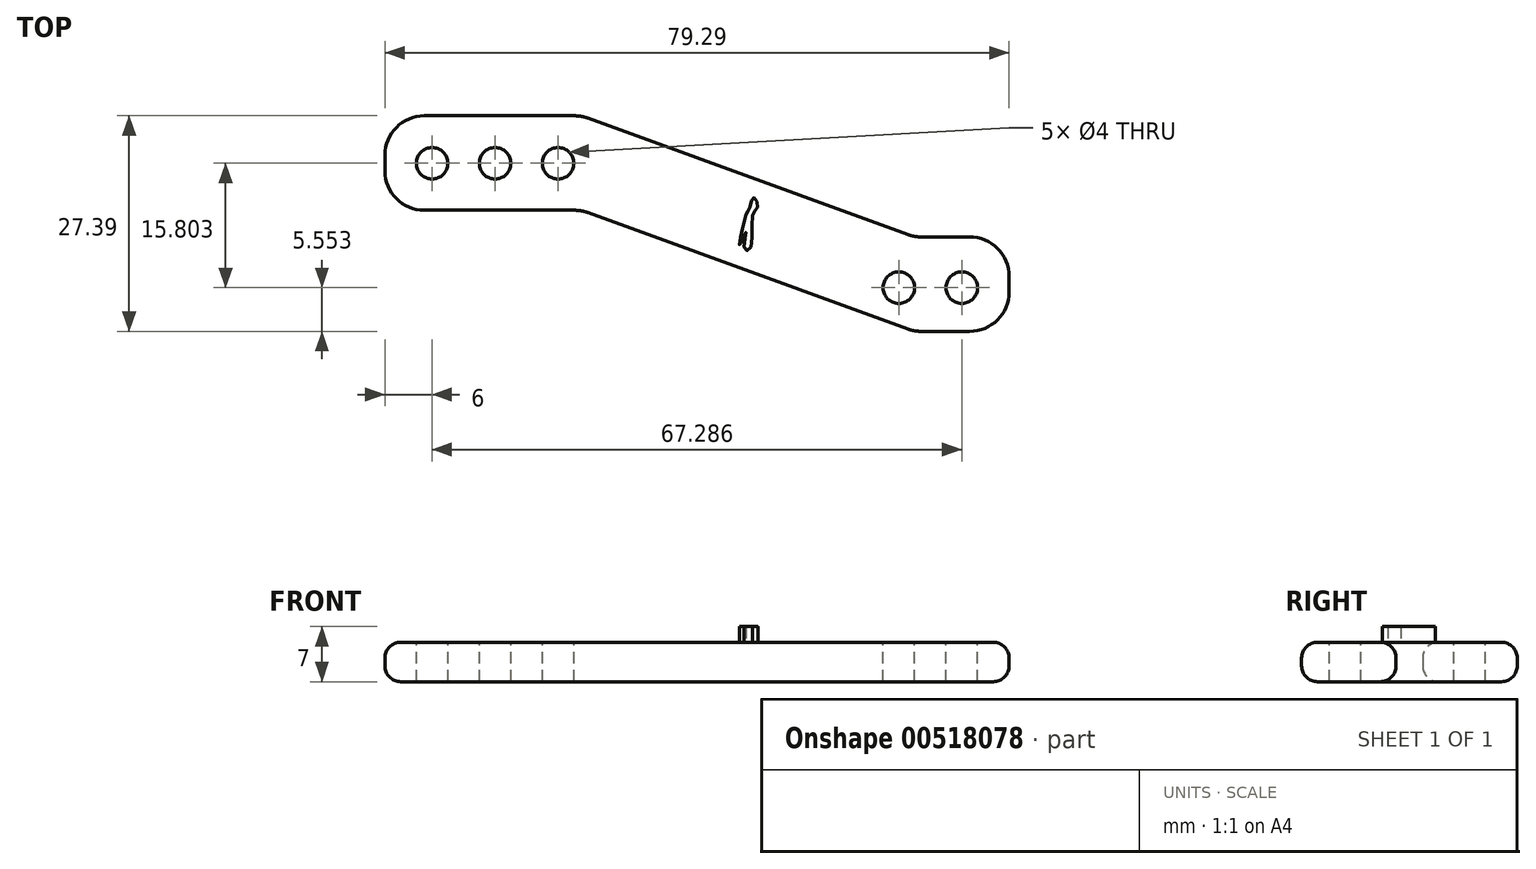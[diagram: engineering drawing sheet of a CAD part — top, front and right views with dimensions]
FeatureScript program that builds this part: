
annotation { "Feature Type Name" : "Feature", "Feature Type Description" : "" }
export const myFeature = defineFeature(function(context is Context, id is Id, definition is map)
    precondition{}
    {
        {
            var Q0;
            Q0=qCreatedBy(makeId("Top.planeOp"),FACE);
            var sketch = newSketch(context, id + "F0", { "sketchPlane" : qUnion([Q0])});
            skLineSegment(sketch, "E0.bottom", {"start": v(0, 0) * mm, "end": v(25, 0) * mm});
            skLineSegment(sketch, "E0.top", {"start": v(0, -12) * mm, "end": v(25, -12) * mm});
            skLineSegment(sketch, "E0.left", {"start": v(0, 0) * mm, "end": v(0, -12) * mm});
            skLineSegment(sketch, "E0.right", {"start": v(25, 0) * mm, "end": v(25, -12) * mm});
            skLineSegment(sketch, "E1", {"start": v(25, -12) * mm, "end": v(67.29, -27.4) * mm});
            skLineSegment(sketch, "E2", {"start": v(25, 0) * mm, "end": v(67.29, -15.4) * mm});
            skLineSegment(sketch, "E3.bottom", {"start": v(67.29, -15.4) * mm, "end": v(79.29, -15.4) * mm});
            skLineSegment(sketch, "E3.top", {"start": v(67.29, -27.4) * mm, "end": v(79.29, -27.4) * mm});
            skLineSegment(sketch, "E3.left", {"start": v(67.29, -15.4) * mm, "end": v(67.29, -27.4) * mm});
            skLineSegment(sketch, "E3.right", {"start": v(79.29, -15.4) * mm, "end": v(79.29, -27.4) * mm});
            skSolve(sketch);
        }
        {
            var Q0;
            Q0=makeQuery(id+"F0.imprint","IMPRINT",FACE,{"disambiguationData":[TD([[makeQuery(id+"F0.imprint","IMPRINT",EDGE,{"derivedFrom":sQuery(id+"F0.wireOp",EDGE,"E0.bottom")}),-1.0]])]});
            var Q1;
            Q1=makeQuery(id+"F0.imprint","IMPRINT",FACE,{"disambiguationData":[TD([[makeQuery(id+"F0.imprint","IMPRINT",EDGE,{"derivedFrom":sQuery(id+"F0.wireOp",EDGE,"E0.right")}),1.0]])]});
            var Q2;
            Q2=makeQuery(id+"F0.imprint","IMPRINT",FACE,{"disambiguationData":[TD([[makeQuery(id+"F0.imprint","IMPRINT",EDGE,{"derivedFrom":sQuery(id+"F0.wireOp",EDGE,"E3.bottom")}),-1.0]])]});
            extrude(context, id + "F1", {"entities" : qUnion([Q0, Q1, Q2]), "depth" : 5 * mm, "offsetDistance" : 25 * mm});
        }
        {
            var Q0;
            Q0=makeQuery(id+"F1.opExtrude","CAP_FACE",FACE,{"disambiguationData":[OSD([sQuery(id+"F0.wireOp",EDGE,"E0.bottom"),sQuery(id+"F0.wireOp",EDGE,"E0.top"),sQuery(id+"F0.wireOp",EDGE,"E0.left"),sQuery(id+"F0.wireOp",EDGE,"E1"),sQuery(id+"F0.wireOp",EDGE,"E2"),sQuery(id+"F0.wireOp",EDGE,"E3.bottom"),sQuery(id+"F0.wireOp",EDGE,"E3.top"),sQuery(id+"F0.wireOp",EDGE,"E3.right")])],"isStart":false});
            var sketch = newSketch(context, id + "F2", { "sketchPlane" : qUnion([Q0])});
            skCircle(sketch, "E4", {"center": v(6, -6.03) * mm, "radius": 2 * mm});
            skCircle(sketch, "E5", {"center": v(73.29, -21.84) * mm, "radius": 2 * mm});
            skCircle(sketch, "E6.1.0.0", {"center": v(14, -6.03) * mm, "radius": 2 * mm});
            skCircle(sketch, "E6.2.0.0", {"center": v(22, -6.03) * mm, "radius": 2 * mm});
            skLineSegment(sketch, "E6.direction1", {"start": v(6, -6.03) * mm, "end": v(14, -6.03) * mm, "construction": true});
            skCircle(sketch, "E7.1.0.0", {"center": v(65.29, -21.84) * mm, "radius": 2 * mm});
            skLineSegment(sketch, "E7.direction1", {"start": v(73.29, -21.84) * mm, "end": v(65.29, -21.84) * mm, "construction": true});
            skSolve(sketch);
        }
        {
            var Q0;
            Q0=makeQuery(id+"F2.imprint","IMPRINT",FACE,{"disambiguationData":[TD([[makeQuery(id+"F2.imprint","IMPRINT",EDGE,{"derivedFrom":sQuery(id+"F2.wireOp",EDGE,"E4")}),1.0]])]});
            var Q1;
            Q1=makeQuery(id+"F2.imprint","IMPRINT",FACE,{"disambiguationData":[TD([[makeQuery(id+"F2.imprint","IMPRINT",EDGE,{"derivedFrom":sQuery(id+"F2.wireOp",EDGE,"E6.1.0.0")}),1.0]])]});
            var Q2;
            Q2=makeQuery(id+"F2.imprint","IMPRINT",FACE,{"disambiguationData":[TD([[makeQuery(id+"F2.imprint","IMPRINT",EDGE,{"derivedFrom":sQuery(id+"F2.wireOp",EDGE,"E6.2.0.0")}),1.0]])]});
            var Q3;
            Q3=makeQuery(id+"F2.imprint","IMPRINT",FACE,{"disambiguationData":[TD([[makeQuery(id+"F2.imprint","IMPRINT",EDGE,{"derivedFrom":sQuery(id+"F2.wireOp",EDGE,"E7.1.0.0")}),1.0]])]});
            var Q4;
            Q4=makeQuery(id+"F2.imprint","IMPRINT",FACE,{"disambiguationData":[TD([[makeQuery(id+"F2.imprint","IMPRINT",EDGE,{"derivedFrom":sQuery(id+"F2.wireOp",EDGE,"E5")}),1.0]])]});
            extrude(context, id + "F3", {"entities" : qUnion([Q0, Q1, Q2, Q3, Q4]), "operationType" : NewBodyOperationType.REMOVE, "endBound" : BoundingType.THROUGH_ALL, "oppositeDirection" : true, "depth" : 25 * mm, "offsetDistance" : 25 * mm});
        }
        {
            var Q0;
            Q0=makeQuery(id+"F1.opExtrude","SWEPT_EDGE",EDGE,{"disambiguationData":[OSD([sQuery(id+"F0.wireOp",EDGE,"E0.top"),sQuery(id+"F0.wireOp",EDGE,"E0.left")])]});
            var Q1;
            Q1=makeQuery(id+"F1.opExtrude","SWEPT_EDGE",EDGE,{"disambiguationData":[OSD([sQuery(id+"F0.wireOp",EDGE,"E0.top"),sQuery(id+"F0.wireOp",EDGE,"E0.right"),sQuery(id+"F0.wireOp",EDGE,"E1")])]});
            var Q2;
            Q2=makeQuery(id+"F1.opExtrude","SWEPT_EDGE",EDGE,{"disambiguationData":[OSD([sQuery(id+"F0.wireOp",EDGE,"E1"),sQuery(id+"F0.wireOp",EDGE,"E3.top"),sQuery(id+"F0.wireOp",EDGE,"E3.left")])]});
            var Q3;
            Q3=makeQuery(id+"F1.opExtrude","SWEPT_EDGE",EDGE,{"disambiguationData":[OSD([sQuery(id+"F0.wireOp",EDGE,"E3.top"),sQuery(id+"F0.wireOp",EDGE,"E3.right")])]});
            var Q4;
            Q4=makeQuery(id+"F1.opExtrude","SWEPT_EDGE",EDGE,{"disambiguationData":[OSD([sQuery(id+"F0.wireOp",EDGE,"E3.bottom"),sQuery(id+"F0.wireOp",EDGE,"E3.right")])]});
            var Q5;
            Q5=makeQuery(id+"F1.opExtrude","SWEPT_EDGE",EDGE,{"disambiguationData":[OSD([sQuery(id+"F0.wireOp",EDGE,"E2"),sQuery(id+"F0.wireOp",EDGE,"E3.bottom"),sQuery(id+"F0.wireOp",EDGE,"E3.left")])]});
            var Q6;
            Q6=makeQuery(id+"F1.opExtrude","SWEPT_EDGE",EDGE,{"disambiguationData":[OSD([sQuery(id+"F0.wireOp",EDGE,"E0.bottom"),sQuery(id+"F0.wireOp",EDGE,"E0.right"),sQuery(id+"F0.wireOp",EDGE,"E2")])]});
            var Q7;
            Q7=makeQuery(id+"F1.opExtrude","SWEPT_EDGE",EDGE,{"disambiguationData":[OSD([sQuery(id+"F0.wireOp",EDGE,"E0.bottom"),sQuery(id+"F0.wireOp",EDGE,"E0.left")])]});
            fillet(context, id + "F4", {"entities" : qUnion([Q0, Q1, Q2, Q3, Q4, Q5, Q6, Q7]), "radius" : 5 * mm, "tangentPropagation" : true, "allowEdgeOverflow" : false});
        }
        {
            var Q0;
            Q0=makeQuery(id+"F1.opExtrude","CAP_EDGE",EDGE,{"disambiguationData":[OSD([sQuery(id+"F0.wireOp",EDGE,"E1")])],"isStart":false});
            var Q1;
            Q1=makeQuery(id+"F1.opExtrude","CAP_EDGE",EDGE,{"disambiguationData":[OSD([sQuery(id+"F0.wireOp",EDGE,"E0.top")])],"isStart":false});
            var Q2;
            Q2=makeQuery(id+"F1.opExtrude","CAP_EDGE",EDGE,{"disambiguationData":[OSD([sQuery(id+"F0.wireOp",EDGE,"E2")])],"isStart":false});
            var Q3;
            Q3=makeQuery(id+"F1.opExtrude","CAP_EDGE",EDGE,{"disambiguationData":[OSD([sQuery(id+"F0.wireOp",EDGE,"E0.bottom")])],"isStart":false});
            var Q4;
            Q4=makeQuery(id+"F1.opExtrude","CAP_EDGE",EDGE,{"disambiguationData":[OSD([sQuery(id+"F0.wireOp",EDGE,"E3.top")])],"isStart":false});
            var Q5;
            Q5=makeQuery(id+"F1.opExtrude","CAP_EDGE",EDGE,{"disambiguationData":[OSD([sQuery(id+"F0.wireOp",EDGE,"E3.bottom")])],"isStart":true});
            var Q6;
            Q6=makeQuery(id+"F1.opExtrude","CAP_EDGE",EDGE,{"disambiguationData":[OSD([sQuery(id+"F0.wireOp",EDGE,"E1")])],"isStart":true});
            var Q7;
            Q7=makeQuery(id+"F1.opExtrude","CAP_EDGE",EDGE,{"disambiguationData":[OSD([sQuery(id+"F0.wireOp",EDGE,"E0.top")])],"isStart":true});
            var Q8;
            {var subQ0=sQuery(id+"F0.wireOp",EDGE,"E0.left");var subQ1=sQuery(id+"F0.wireOp",EDGE,"E0.top");Q8=makeQuery(id+"F4.opFillet","BLEND_EDGE",EDGE,{"blendedFrom":[makeQuery(id+"F1.opExtrude","SWEPT_EDGE",EDGE,{"disambiguationData":[OSD([subQ1,subQ0])]}),makeQuery(id+"F1.opExtrude","CAP_FACE",FACE,{"disambiguationData":[OSD([sQuery(id+"F0.wireOp",EDGE,"E0.bottom"),subQ1,subQ0,sQuery(id+"F0.wireOp",EDGE,"E1"),sQuery(id+"F0.wireOp",EDGE,"E2"),sQuery(id+"F0.wireOp",EDGE,"E3.bottom"),sQuery(id+"F0.wireOp",EDGE,"E3.top"),sQuery(id+"F0.wireOp",EDGE,"E3.right")])],"isStart":false})],"blendedInto":[makeQuery(id+"F1.opExtrude","CAP_FACE",FACE,{"disambiguationData":[OSD([sQuery(id+"F0.wireOp",EDGE,"E0.bottom"),subQ1,subQ0,sQuery(id+"F0.wireOp",EDGE,"E1"),sQuery(id+"F0.wireOp",EDGE,"E2"),sQuery(id+"F0.wireOp",EDGE,"E3.bottom"),sQuery(id+"F0.wireOp",EDGE,"E3.top"),sQuery(id+"F0.wireOp",EDGE,"E3.right")])],"isStart":false})]});}
            var Q9;
            {var subQ0=sQuery(id+"F0.wireOp",EDGE,"E3.right");var subQ1=sQuery(id+"F0.wireOp",EDGE,"E3.top");Q9=makeQuery(id+"F4.opFillet","BLEND_EDGE",EDGE,{"blendedFrom":[makeQuery(id+"F1.opExtrude","SWEPT_EDGE",EDGE,{"disambiguationData":[OSD([subQ1,subQ0])]}),makeQuery(id+"F1.opExtrude","CAP_FACE",FACE,{"disambiguationData":[OSD([sQuery(id+"F0.wireOp",EDGE,"E0.bottom"),sQuery(id+"F0.wireOp",EDGE,"E0.top"),sQuery(id+"F0.wireOp",EDGE,"E0.left"),sQuery(id+"F0.wireOp",EDGE,"E1"),sQuery(id+"F0.wireOp",EDGE,"E2"),sQuery(id+"F0.wireOp",EDGE,"E3.bottom"),subQ1,subQ0])],"isStart":false})],"blendedInto":[makeQuery(id+"F1.opExtrude","CAP_FACE",FACE,{"disambiguationData":[OSD([sQuery(id+"F0.wireOp",EDGE,"E0.bottom"),sQuery(id+"F0.wireOp",EDGE,"E0.top"),sQuery(id+"F0.wireOp",EDGE,"E0.left"),sQuery(id+"F0.wireOp",EDGE,"E1"),sQuery(id+"F0.wireOp",EDGE,"E2"),sQuery(id+"F0.wireOp",EDGE,"E3.bottom"),subQ1,subQ0])],"isStart":false})]});}
            var Q10;
            {var subQ0=sQuery(id+"F0.wireOp",EDGE,"E0.left");var subQ1=sQuery(id+"F0.wireOp",EDGE,"E0.top");Q10=makeQuery(id+"F4.opFillet","BLEND_EDGE",EDGE,{"blendedFrom":[makeQuery(id+"F1.opExtrude","SWEPT_EDGE",EDGE,{"disambiguationData":[OSD([subQ1,subQ0])]}),makeQuery(id+"F1.opExtrude","CAP_FACE",FACE,{"disambiguationData":[OSD([sQuery(id+"F0.wireOp",EDGE,"E0.bottom"),subQ1,subQ0,sQuery(id+"F0.wireOp",EDGE,"E1"),sQuery(id+"F0.wireOp",EDGE,"E2"),sQuery(id+"F0.wireOp",EDGE,"E3.bottom"),sQuery(id+"F0.wireOp",EDGE,"E3.top"),sQuery(id+"F0.wireOp",EDGE,"E3.right")])],"isStart":true})],"blendedInto":[makeQuery(id+"F1.opExtrude","CAP_FACE",FACE,{"disambiguationData":[OSD([sQuery(id+"F0.wireOp",EDGE,"E0.bottom"),subQ1,subQ0,sQuery(id+"F0.wireOp",EDGE,"E1"),sQuery(id+"F0.wireOp",EDGE,"E2"),sQuery(id+"F0.wireOp",EDGE,"E3.bottom"),sQuery(id+"F0.wireOp",EDGE,"E3.top"),sQuery(id+"F0.wireOp",EDGE,"E3.right")])],"isStart":true})]});}
            var Q11;
            {var subQ0=sQuery(id+"F0.wireOp",EDGE,"E3.right");var subQ1=sQuery(id+"F0.wireOp",EDGE,"E3.top");Q11=makeQuery(id+"F4.opFillet","BLEND_EDGE",EDGE,{"blendedFrom":[makeQuery(id+"F1.opExtrude","SWEPT_EDGE",EDGE,{"disambiguationData":[OSD([subQ1,subQ0])]}),makeQuery(id+"F1.opExtrude","CAP_FACE",FACE,{"disambiguationData":[OSD([sQuery(id+"F0.wireOp",EDGE,"E0.bottom"),sQuery(id+"F0.wireOp",EDGE,"E0.top"),sQuery(id+"F0.wireOp",EDGE,"E0.left"),sQuery(id+"F0.wireOp",EDGE,"E1"),sQuery(id+"F0.wireOp",EDGE,"E2"),sQuery(id+"F0.wireOp",EDGE,"E3.bottom"),subQ1,subQ0])],"isStart":true})],"blendedInto":[makeQuery(id+"F1.opExtrude","CAP_FACE",FACE,{"disambiguationData":[OSD([sQuery(id+"F0.wireOp",EDGE,"E0.bottom"),sQuery(id+"F0.wireOp",EDGE,"E0.top"),sQuery(id+"F0.wireOp",EDGE,"E0.left"),sQuery(id+"F0.wireOp",EDGE,"E1"),sQuery(id+"F0.wireOp",EDGE,"E2"),sQuery(id+"F0.wireOp",EDGE,"E3.bottom"),subQ1,subQ0])],"isStart":true})]});}
            var Q12;
            {var subQ0=sQuery(id+"F0.wireOp",EDGE,"E3.right");var subQ1=sQuery(id+"F0.wireOp",EDGE,"E3.bottom");Q12=makeQuery(id+"F4.opFillet","BLEND_EDGE",EDGE,{"blendedFrom":[makeQuery(id+"F1.opExtrude","SWEPT_EDGE",EDGE,{"disambiguationData":[OSD([subQ1,subQ0])]}),makeQuery(id+"F1.opExtrude","CAP_FACE",FACE,{"disambiguationData":[OSD([sQuery(id+"F0.wireOp",EDGE,"E0.bottom"),sQuery(id+"F0.wireOp",EDGE,"E0.top"),sQuery(id+"F0.wireOp",EDGE,"E0.left"),sQuery(id+"F0.wireOp",EDGE,"E1"),sQuery(id+"F0.wireOp",EDGE,"E2"),subQ1,sQuery(id+"F0.wireOp",EDGE,"E3.top"),subQ0])],"isStart":true})],"blendedInto":[makeQuery(id+"F1.opExtrude","CAP_FACE",FACE,{"disambiguationData":[OSD([sQuery(id+"F0.wireOp",EDGE,"E0.bottom"),sQuery(id+"F0.wireOp",EDGE,"E0.top"),sQuery(id+"F0.wireOp",EDGE,"E0.left"),sQuery(id+"F0.wireOp",EDGE,"E1"),sQuery(id+"F0.wireOp",EDGE,"E2"),subQ1,sQuery(id+"F0.wireOp",EDGE,"E3.top"),subQ0])],"isStart":true})]});}
            var Q13;
            {var subQ0=sQuery(id+"F0.wireOp",EDGE,"E3.right");var subQ1=sQuery(id+"F0.wireOp",EDGE,"E3.bottom");Q13=makeQuery(id+"F4.opFillet","BLEND_EDGE",EDGE,{"blendedFrom":[makeQuery(id+"F1.opExtrude","SWEPT_EDGE",EDGE,{"disambiguationData":[OSD([subQ1,subQ0])]}),makeQuery(id+"F1.opExtrude","CAP_FACE",FACE,{"disambiguationData":[OSD([sQuery(id+"F0.wireOp",EDGE,"E0.bottom"),sQuery(id+"F0.wireOp",EDGE,"E0.top"),sQuery(id+"F0.wireOp",EDGE,"E0.left"),sQuery(id+"F0.wireOp",EDGE,"E1"),sQuery(id+"F0.wireOp",EDGE,"E2"),subQ1,sQuery(id+"F0.wireOp",EDGE,"E3.top"),subQ0])],"isStart":false})],"blendedInto":[makeQuery(id+"F1.opExtrude","CAP_FACE",FACE,{"disambiguationData":[OSD([sQuery(id+"F0.wireOp",EDGE,"E0.bottom"),sQuery(id+"F0.wireOp",EDGE,"E0.top"),sQuery(id+"F0.wireOp",EDGE,"E0.left"),sQuery(id+"F0.wireOp",EDGE,"E1"),sQuery(id+"F0.wireOp",EDGE,"E2"),subQ1,sQuery(id+"F0.wireOp",EDGE,"E3.top"),subQ0])],"isStart":false})]});}
            var Q14;
            {var subQ0=sQuery(id+"F0.wireOp",EDGE,"E3.bottom");var subQ1=sQuery(id+"F0.wireOp",EDGE,"E2");Q14=makeQuery(id+"F4.opFillet","BLEND_EDGE",EDGE,{"blendedFrom":[makeQuery(id+"F1.opExtrude","SWEPT_EDGE",EDGE,{"disambiguationData":[OSD([subQ1,subQ0,sQuery(id+"F0.wireOp",EDGE,"E3.left")])]}),makeQuery(id+"F1.opExtrude","CAP_FACE",FACE,{"disambiguationData":[OSD([sQuery(id+"F0.wireOp",EDGE,"E0.bottom"),sQuery(id+"F0.wireOp",EDGE,"E0.top"),sQuery(id+"F0.wireOp",EDGE,"E0.left"),sQuery(id+"F0.wireOp",EDGE,"E1"),subQ1,subQ0,sQuery(id+"F0.wireOp",EDGE,"E3.top"),sQuery(id+"F0.wireOp",EDGE,"E3.right")])],"isStart":false})],"blendedInto":[makeQuery(id+"F1.opExtrude","CAP_FACE",FACE,{"disambiguationData":[OSD([sQuery(id+"F0.wireOp",EDGE,"E0.bottom"),sQuery(id+"F0.wireOp",EDGE,"E0.top"),sQuery(id+"F0.wireOp",EDGE,"E0.left"),sQuery(id+"F0.wireOp",EDGE,"E1"),subQ1,subQ0,sQuery(id+"F0.wireOp",EDGE,"E3.top"),sQuery(id+"F0.wireOp",EDGE,"E3.right")])],"isStart":false})]});}
            var Q15;
            {var subQ0=sQuery(id+"F0.wireOp",EDGE,"E2");var subQ1=sQuery(id+"F0.wireOp",EDGE,"E0.bottom");Q15=makeQuery(id+"F4.opFillet","BLEND_EDGE",EDGE,{"blendedFrom":[makeQuery(id+"F1.opExtrude","SWEPT_EDGE",EDGE,{"disambiguationData":[OSD([subQ1,sQuery(id+"F0.wireOp",EDGE,"E0.right"),subQ0])]}),makeQuery(id+"F1.opExtrude","CAP_FACE",FACE,{"disambiguationData":[OSD([subQ1,sQuery(id+"F0.wireOp",EDGE,"E0.top"),sQuery(id+"F0.wireOp",EDGE,"E0.left"),sQuery(id+"F0.wireOp",EDGE,"E1"),subQ0,sQuery(id+"F0.wireOp",EDGE,"E3.bottom"),sQuery(id+"F0.wireOp",EDGE,"E3.top"),sQuery(id+"F0.wireOp",EDGE,"E3.right")])],"isStart":false})],"blendedInto":[makeQuery(id+"F1.opExtrude","CAP_FACE",FACE,{"disambiguationData":[OSD([subQ1,sQuery(id+"F0.wireOp",EDGE,"E0.top"),sQuery(id+"F0.wireOp",EDGE,"E0.left"),sQuery(id+"F0.wireOp",EDGE,"E1"),subQ0,sQuery(id+"F0.wireOp",EDGE,"E3.bottom"),sQuery(id+"F0.wireOp",EDGE,"E3.top"),sQuery(id+"F0.wireOp",EDGE,"E3.right")])],"isStart":false})]});}
            var Q16;
            {var subQ0=sQuery(id+"F0.wireOp",EDGE,"E0.left");var subQ1=sQuery(id+"F0.wireOp",EDGE,"E0.bottom");Q16=makeQuery(id+"F4.opFillet","BLEND_EDGE",EDGE,{"blendedFrom":[makeQuery(id+"F1.opExtrude","SWEPT_EDGE",EDGE,{"disambiguationData":[OSD([subQ1,subQ0])]}),makeQuery(id+"F1.opExtrude","CAP_FACE",FACE,{"disambiguationData":[OSD([subQ1,sQuery(id+"F0.wireOp",EDGE,"E0.top"),subQ0,sQuery(id+"F0.wireOp",EDGE,"E1"),sQuery(id+"F0.wireOp",EDGE,"E2"),sQuery(id+"F0.wireOp",EDGE,"E3.bottom"),sQuery(id+"F0.wireOp",EDGE,"E3.top"),sQuery(id+"F0.wireOp",EDGE,"E3.right")])],"isStart":false})],"blendedInto":[makeQuery(id+"F1.opExtrude","CAP_FACE",FACE,{"disambiguationData":[OSD([subQ1,sQuery(id+"F0.wireOp",EDGE,"E0.top"),subQ0,sQuery(id+"F0.wireOp",EDGE,"E1"),sQuery(id+"F0.wireOp",EDGE,"E2"),sQuery(id+"F0.wireOp",EDGE,"E3.bottom"),sQuery(id+"F0.wireOp",EDGE,"E3.top"),sQuery(id+"F0.wireOp",EDGE,"E3.right")])],"isStart":false})]});}
            var Q17;
            Q17=makeQuery(id+"F1.opExtrude","CAP_EDGE",EDGE,{"disambiguationData":[OSD([sQuery(id+"F0.wireOp",EDGE,"E3.bottom")])],"isStart":false});
            var Q18;
            Q18=makeQuery(id+"F1.opExtrude","CAP_EDGE",EDGE,{"disambiguationData":[OSD([sQuery(id+"F0.wireOp",EDGE,"E0.bottom")])],"isStart":true});
            var Q19;
            Q19=makeQuery(id+"F1.opExtrude","CAP_EDGE",EDGE,{"disambiguationData":[OSD([sQuery(id+"F0.wireOp",EDGE,"E2")])],"isStart":true});
            fillet(context, id + "F5", {"entities" : qUnion([Q0, Q1, Q2, Q3, Q4, Q5, Q6, Q7, Q8, Q9, Q10, Q11, Q12, Q13, Q14, Q15, Q16, Q17, Q18, Q19]), "radius" : 2 * mm, "tangentPropagation" : true, "allowEdgeOverflow" : false});
        }
        {
            var Q0;
            Q0=makeQuery(id+"F1.opExtrude","CAP_FACE",FACE,{"disambiguationData":[OSD([sQuery(id+"F0.wireOp",EDGE,"E0.bottom"),sQuery(id+"F0.wireOp",EDGE,"E0.top"),sQuery(id+"F0.wireOp",EDGE,"E0.left"),sQuery(id+"F0.wireOp",EDGE,"E1"),sQuery(id+"F0.wireOp",EDGE,"E2"),sQuery(id+"F0.wireOp",EDGE,"E3.bottom"),sQuery(id+"F0.wireOp",EDGE,"E3.top"),sQuery(id+"F0.wireOp",EDGE,"E3.right")])],"isStart":false});
            var sketch = newSketch(context, id + "F6", { "sketchPlane" : qUnion([Q0])});
            skPoint(sketch, "E8.5.internal.snap0", {"position": v(45.07, -17.18) * mm});
            skFitSpline(sketch, "E8", {"points": [v(47.36, -11.67) * mm, v(46.8, -12.3) * mm, v(46.41, -16.84) * mm, v(45.7, -16.93) * mm, v(45.85, -14.8) * mm, v(45.07, -16.45) * mm, v(45.48, -14.2) * mm, v(45.74, -13.08) * mm, v(45.98, -12.35) * mm, v(46.4, -11.48) * mm, v(46.88, -10.39) * mm, v(47.36, -11.67) * mm]});
            skSolve(sketch);
        }
        {
            var Q0;
            Q0=makeQuery(id+"F6.imprint","IMPRINT",FACE,{"disambiguationData":[TD([[makeQuery(id+"F6.imprint","IMPRINT",EDGE,{"derivedFrom":sQuery(id+"F6.wireOp",EDGE,"E8")}),-1.0]])]});
            extrude(context, id + "F7", {"entities" : qUnion([Q0]), "operationType" : NewBodyOperationType.ADD, "depth" : 2 * mm, "offsetDistance" : 25 * mm});
        }
    });
